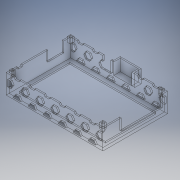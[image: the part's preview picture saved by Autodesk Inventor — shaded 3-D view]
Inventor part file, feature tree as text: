
AUTODESK INVENTOR PART (.ipt)
format: ipt  version: 2017 (Build 210142000, 142)  size: 1,347,584 bytes
history: native  units: mm
features: extrude x28, sketch x27, projected_geometry x22, draft x2, chamfer x1
ambient origin geometry x8: Origin, YZ Plane, XZ Plane, XY Plane, X Axis, Y Axis, Z Axis, Center Point
bodies: Solid1 (feature_tree)
feature tree (80):
  extrude  "Extrusion1"  Depth=3.0mm
  extrude  "Extrusion2"  Depth=56.0mm
  draft  "FaceDraft1"
  draft  "FaceDraft2"
  extrude  "Extrusion3"  Depth=3.5mm
  extrude  "Extrusion4"  Depth=2.75mm
  extrude  "Extrusion5"  Depth=2.75mm
  extrude  "Extrusion7"  Depth=0.5mm
  extrude  "Extrusion8"  Depth=0.5mm
  extrude  "Extrusion9"  Depth=24.0mm
  extrude  "Extrusion10"  Depth=5.5mm
  extrude  "Extrusion11"  Depth=2.0mm TaperAngle=0.0deg
  extrude  "Extrusion12"  Depth=49.0mm
  extrude  "Extrusion13"  Depth=69.5mm
  extrude  "Extrusion14"  Depth=92.45mm
  extrude  "Extrusion15"  Depth=69.5mm
  extrude  "Extrusion16"  Depth=2.75mm
  extrude  "Extrusion17"  Depth=21.0mm
  extrude  "Extrusion18"  Depth=88.0mm
  extrude  "Extrusion25"  Depth=6.0mm
  extrude  "Extrusion27"  Depth=6.0mm
  extrude  "Extrusion28"  Depth=3.0mm TaperAngle=0.0deg
  extrude  "Extrusion29"  TaperAngle=15.0deg  [1 undecoded]
  extrude  "Extrusion32"  Depth=6.0mm
  extrude  "Extrusion33"  Depth=6.0mm
  extrude  "Extrusion35"  Depth=5.5mm
  extrude  "Extrusion37"  Depth=1.0mm
  extrude  "Extrusion38"  Depth=88.0mm TaperAngle=0.0deg
  extrude  "Extrusion39"  Depth=28.0mm
  extrude  "Extrusion42"  Depth=2.0mm
  chamfer  "Chamfer3"  Distance=4.25mm
  sketch  "Sketch1"  dims[d1=78.0mm d3=3.0mm]
  sketch  "Sketch2"  dims[d7=85.0mm d8=56.0mm]
  sketch  "Sketch3"  dims[d9=3.5mm d10=3.5mm]
  sketch  "Sketch4"  dims[d11=49.0mm d12=2.75mm]
  sketch  "Sketch5"  dims[d13=2.75mm d14=2.75mm]
  sketch  "Sketch8"  dims[d21=0.5mm d22=0.5mm]
  projected_geometry  "Projected Loop1"
  sketch  "Sketch9"  dims[d23=0.5mm d24=32.0mm]
  projected_geometry  "Projected Loop2"
  sketch  "Sketch10"  dims[d25=12.0mm d28=24.0mm]
  sketch  "Sketch11"  dims[d29=10.6mm d30=5.5mm]
  sketch  "Sketch13"  dims[d31=11.0mm d32=2.0mm d33=2.0mm d34=0.0mm]
  projected_geometry  "Projected Loop3"
  projected_geometry  "Projected Loop4"
  projected_geometry  "Projected Loop5"
  sketch  "Sketch15"  dims[d45=58.0mm d46=49.0mm]
  sketch  "Sketch16"  dims[d47=2.75mm d48=69.5mm]
  sketch  "Sketch17"  dims[d49=90.0deg d50=92.45mm]
  sketch  "Sketch18"  dims[d51=90.0deg d52=69.5mm]
  projected_geometry  "Projected Loop10"
  projected_geometry  "Projected Loop11"
  projected_geometry  "Projected Loop12"
  projected_geometry  "Projected Loop13"
  sketch  "Sketch20"  dims[d53=90.0deg d55=2.75mm]
  sketch  "Sketch21"  dims[d56=1.0mm d57=21.0mm]
  sketch  "Sketch29"  dims[d64=5.1mm d65=88.0mm]
  sketch  "Sketch33"  dims[d66=90.0deg d67=6.0mm]
  projected_geometry  "Projected Loop20"
  sketch  "Sketch34"  dims[d68=6.0mm d69=6.0mm]
  projected_geometry  "Projected Loop21"
  sketch  "Sketch35"  dims[d70=6.0mm d71=3.0mm d72=0.0mm]
  projected_geometry  "Projected Loop22"
  projected_geometry  "Projected Loop23"
  projected_geometry  "Projected Loop24"
  sketch  "Sketch38"  dims[d73=15.0deg d74=15.0deg]
  sketch  "Sketch39"  dims[d111=2.75mm d112=6.0mm]
  projected_geometry  "Projected Loop27"
  sketch  "Sketch41"  dims[d113=6.0mm d114=6.0mm]
  projected_geometry  "Projected Loop33"
  projected_geometry  "Projected Loop34"
  projected_geometry  "Projected Loop35"
  projected_geometry  "Projected Loop36"
  projected_geometry  "Projected Loop37"
  sketch  "Sketch43"  dims[d152=6.0mm d153=0.0mm d154=5.5mm]
  sketch  "Sketch44"  dims[d155=1.0mm d156=1.0mm]
  projected_geometry  "Projected Loop42"
  sketch  "Sketch45"  dims[d157=88.0mm d158=0.0mm d159=14.0mm d160=0.0mm]
  projected_geometry  "Projected Loop46"
  sketch  "Sketch48"  dims[d163=2.75mm d172=28.0mm d180=2.0mm d181=4.25mm d182=0.0mm d183=1.0mm d184=1.0mm d185=11.0mm d186=15.98mm d187=0.0mm d188=1.0mm d189=1.0mm d190=11.0mm d191=16.23mm d192=0.0mm d193=7.36mm d194=1.0mm d195=2.0mm d196=0.0mm d197=4.3mm d199=3.0mm d200=2.0mm d201=4.6mm d202=0.0mm d203=2.0mm d204=0.0mm d205=4.3mm d206=3.0mm d207=2.0mm d208=10.0mm d209=0.0mm d210=1.0mm d211=1.0mm d212=11.0mm d213=0.5mm d214=0.0mm d215=1.75mm d216=0.0mm d217=8.5mm d218=0.0mm d222=6.5mm d223=0.0mm d226=11.0mm d227=120.7mm d228=5.0mm d229=110.7mm d231=2.1mm d232=67.4mm d233=2.0mm d234=0.0mm d995=5.0mm d996=10.0mm d997=5.0mm d998=10.0mm d999=5.0mm d1000=10.0mm d1001=5.0mm d1002=5.0mm d1003=10.0mm d1004=5.0mm d1005=5.0mm d1006=10.0mm d1007=5.0mm d1008=10.0mm d1009=5.0mm d1010=10.0mm d1011=5.0mm d1012=10.0mm d1013=5.0mm d1014=10.0mm d1015=5.0mm d1016=10.0mm d1017=5.0mm d1018=10.0mm d1019=5.0mm d1020=10.0mm d1021=5.0mm d1022=10.0mm d1023=5.0mm d1024=10.0mm d1025=5.0mm d1026=10.0mm d1027=5.0mm d1028=5.0mm d1029=5.0mm d1030=5.0mm d1031=10.0mm d1032=5.0mm d1033=10.0mm d1034=5.0mm d1035=5.0mm d1036=10.0mm d1037=5.0mm d1038=10.0mm d1039=10.0mm d1040=5.0mm d1041=10.0mm d1042=5.0mm d1043=10.0mm d1044=5.0mm d1045=10.0mm d1046=3.0mm d1047=0.0mm d1050=0.5mm d1051=0.5mm d1054=0.5mm d1055=0.5mm d1056=0.5mm d1057=0.5mm d1058=87.511mm d1059=0.0mm d1060=12.0mm d1061=0.0mm d1062=92.45mm d1063=3.25mm d1064=4.0mm d1065=0.0mm d1067=0.0mm d1068=1.5mm d1069=0.0mm d1082=4.5mm d1083=4.5mm d1085=4.5mm d1086=4.5mm d1087=2.75mm d1088=4.5mm d1089=4.5mm d1090=2.75mm d1091=6.5mm d1092=0.0mm d1093=4.0mm d1094=0.0mm d1097=10.0mm d1098=0.0mm d1144=34.728mm d1145=2.0mm d1146=0.0mm d1147=2.0mm d1148=0.0mm d1149=0.327mm d1150=90.0deg d1151=2.75mm d1152=3.0mm d1153=3.0mm d1154=3.0mm d1156=0.1mm d1158=90.0deg d1159=150.0mm d1160=0.0mm d1193=2.7mm d1194=2.7mm d1195=2.7mm d1196=2.7mm d1197=2.7mm d1198=3.0mm d1199=4.5mm d1200=4.5mm d1201=2.7mm d1202=2.7mm d1203=2.7mm d1204=2.7mm d1205=3.0mm d1206=6.82mm d1207=0.0mm d1208=0.0mm d1209=3.0mm d1210=2.0mm d1211=45.0deg]
note: 1 required parameter value undecoded (feature->parameter linkage not recoverable at this tier; creation-order binding heuristic only, values carry confidence <= 0.55)
